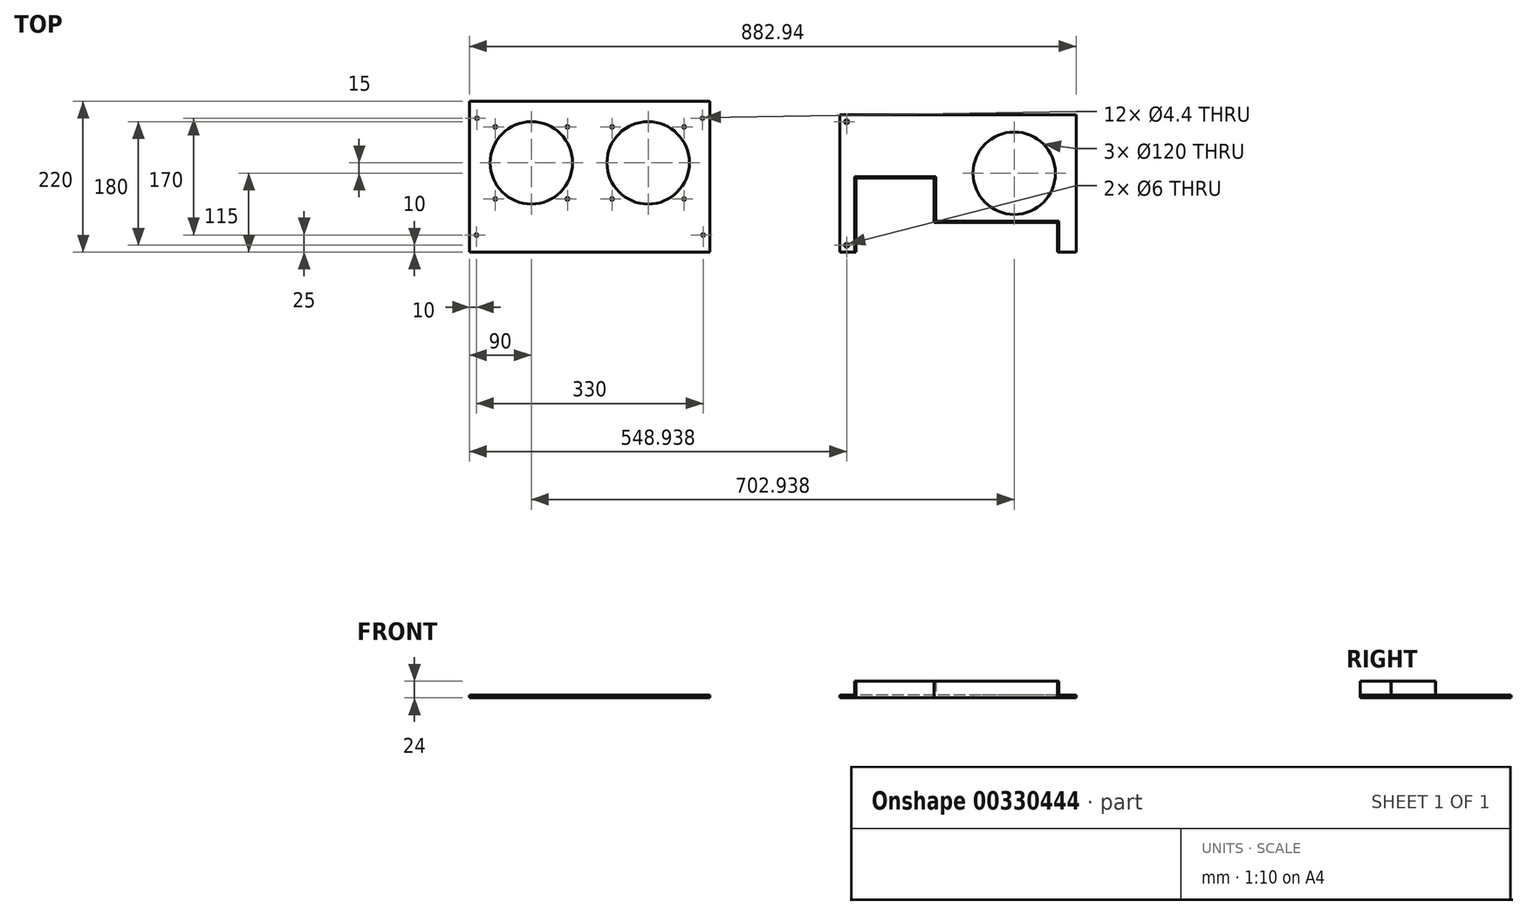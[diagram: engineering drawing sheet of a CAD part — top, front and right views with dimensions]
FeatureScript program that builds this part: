
annotation { "Feature Type Name" : "Feature", "Feature Type Description" : "" }
export const myFeature = defineFeature(function(context is Context, id is Id, definition is map)
    precondition{}
    {
        {
            var Q0;
            Q0=qCreatedBy(makeId("Top.planeOp"),FACE);
            var sketch = newSketch(context, id + "F0", { "sketchPlane" : qUnion([Q0])});
            skLineSegment(sketch, "E0.bottom", {"start": v(0, 0) * mm, "end": v(-350, 0) * mm});
            skLineSegment(sketch, "E0.top", {"start": v(0, 220) * mm, "end": v(-350, 220) * mm});
            skLineSegment(sketch, "E0.left", {"start": v(0, 0) * mm, "end": v(0, 220) * mm});
            skLineSegment(sketch, "E0.right", {"start": v(-350, 0) * mm, "end": v(-350, 220) * mm});
            skPoint(sketch, "E1", {"position": v(-339.2, 220) * mm});
            skPoint(sketch, "E2", {"position": v(-350, 195) * mm});
            skPoint(sketch, "E3", {"position": v(-339.2, 195) * mm});
            skCircle(sketch, "E4", {"center": v(-339.2, 195) * mm, "radius": 2.2 * mm});
            skPoint(sketch, "E5.endSnap0", {"position": v(-350, 110) * mm});
            skCircle(sketch, "E6.MirrorC", {"center": v(-340, 25) * mm, "radius": 2.2 * mm});
            skCircle(sketch, "E7.MirrorC", {"center": v(-10, 25) * mm, "radius": 2.2 * mm});
            skPoint(sketch, "E8.MirrorP", {"position": v(-10.8, 195) * mm});
            skCircle(sketch, "E9.MirrorC", {"center": v(-10.8, 195) * mm, "radius": 2.2 * mm});
            skLineSegment(sketch, "E10", {"start": v(-350, 110) * mm, "end": v(0, 110) * mm, "construction": true});
            skPoint(sketch, "E11", {"position": v(-270, 110) * mm});
            skPoint(sketch, "E12", {"position": v(-80, 110) * mm});
            skCircle(sketch, "E13", {"center": v(-260, 130) * mm, "radius": 60 * mm});
            skCircle(sketch, "E14", {"center": v(-90, 130) * mm, "radius": 60 * mm});
            skLineSegment(sketch, "E15", {"start": v(-260, 130) * mm, "end": v(-260, 220) * mm, "construction": true});
            skLineSegment(sketch, "E16", {"start": v(-260, 130) * mm, "end": v(-232.6, 130) * mm, "construction": true});
            skCircle(sketch, "E17", {"center": v(-312.5, 182.5) * mm, "radius": 2.2 * mm});
            skCircle(sketch, "E18.MirrorC", {"center": v(-207.5, 182.5) * mm, "radius": 2.2 * mm});
            skCircle(sketch, "E19.MirrorC", {"center": v(-312.5, 77.5) * mm, "radius": 2.2 * mm});
            skCircle(sketch, "E20.MirrorC", {"center": v(-207.5, 77.5) * mm, "radius": 2.2 * mm});
            skLineSegment(sketch, "E21", {"start": v(-175, 0) * mm, "end": v(-175, 35.85) * mm, "construction": true});
            skPoint(sketch, "E21.endSnap0", {"position": v(-175, 0) * mm});
            skCircle(sketch, "E22.MirrorC", {"center": v(-142.5, 77.5) * mm, "radius": 2.2 * mm});
            skCircle(sketch, "E23.MirrorC", {"center": v(-142.5, 182.5) * mm, "radius": 2.2 * mm});
            skCircle(sketch, "E24.MirrorC", {"center": v(-37.5, 182.5) * mm, "radius": 2.2 * mm});
            skCircle(sketch, "E25.MirrorC", {"center": v(-37.5, 77.5) * mm, "radius": 2.2 * mm});
            skSolve(sketch);
        }
        {
            var Q0;
            Q0=makeQuery(id+"F0.imprint","IMPRINT",FACE,{"disambiguationData":[TD([[makeQuery(id+"F0.imprint","IMPRINT",EDGE,{"derivedFrom":sQuery(id+"F0.wireOp",EDGE,"E0.bottom")}),-1.0]])]});
            extrude(context, id + "F1", {"entities" : qUnion([Q0]), "depth" : 4 * mm});
        }
        {
            var Q0;
            Q0=qCreatedBy(makeId("Top.planeOp"),FACE);
            var sketch = newSketch(context, id + "F2", { "sketchPlane" : qUnion([Q0])});
            skLineSegment(sketch, "E26.bottom", {"start": v(532.94, 0) * mm, "end": v(188.94, 0) * mm});
            skLineSegment(sketch, "E26.top", {"start": v(532.94, 200) * mm, "end": v(188.94, 200) * mm});
            skLineSegment(sketch, "E26.left", {"start": v(532.94, 0) * mm, "end": v(532.94, 200) * mm});
            skLineSegment(sketch, "E26.right", {"start": v(188.94, 0) * mm, "end": v(188.94, 200) * mm});
            skPoint(sketch, "E27", {"position": v(198.94, 200) * mm});
            skPoint(sketch, "E28", {"position": v(188.94, 190) * mm});
            skPoint(sketch, "E29", {"position": v(198.94, 190) * mm});
            skCircle(sketch, "E30", {"center": v(198.94, 190) * mm, "radius": 3 * mm});
            skPoint(sketch, "E31.endSnap0", {"position": v(360.94, 0) * mm});
            skLineSegment(sketch, "E32", {"start": v(188.94, 100) * mm, "end": v(210.85, 100) * mm, "construction": true});
            skPoint(sketch, "E32.endSnap0", {"position": v(188.94, 100) * mm});
            skCircle(sketch, "E33.MirrorC", {"center": v(198.94, 10) * mm, "radius": 3 * mm});
            skCircle(sketch, "E34.MirrorC", {"center": v(492.94, 10) * mm, "radius": 3 * mm});
            skPoint(sketch, "E35.MirrorP", {"position": v(492.94, 190) * mm});
            skLineSegment(sketch, "E36", {"start": v(507.94, 45) * mm, "end": v(507.94, 0) * mm});
            skLineSegment(sketch, "E37", {"start": v(507.94, 45) * mm, "end": v(328.46, 45) * mm});
            skLineSegment(sketch, "E38", {"start": v(328.46, 45) * mm, "end": v(328.46, 110) * mm});
            skLineSegment(sketch, "E39", {"start": v(328.46, 110) * mm, "end": v(210.44, 110) * mm});
            skLineSegment(sketch, "E40", {"start": v(210.44, 110) * mm, "end": v(210.44, 0) * mm});
            skLineSegment(sketch, "E41.0", {"start": v(212.44, 108) * mm, "end": v(212.44, 0) * mm});
            skLineSegment(sketch, "E41.1", {"start": v(505.94, 43) * mm, "end": v(505.94, 3) * mm});
            skLineSegment(sketch, "E41.2", {"start": v(505.94, 43) * mm, "end": v(326.46, 43) * mm});
            skLineSegment(sketch, "E41.3", {"start": v(326.46, 43) * mm, "end": v(326.46, 108) * mm});
            skLineSegment(sketch, "E41.4", {"start": v(326.46, 108) * mm, "end": v(212.44, 108) * mm});
            skLineSegment(sketch, "E42", {"start": v(505.94, 3) * mm, "end": v(505.94, 0) * mm});
            skPoint(sketch, "E43", {"position": v(507.94, 115) * mm});
            skPoint(sketch, "E44", {"position": v(442.94, 115) * mm});
            skCircle(sketch, "E45", {"center": v(442.94, 115) * mm, "radius": 60 * mm});
            skSolve(sketch);
        }
        {
            var Q0;
            Q0=makeQuery(id+"F2.imprint","IMPRINT",FACE,{"disambiguationData":[TD([[makeQuery(id+"F2.imprint","IMPRINT",EDGE,{"derivedFrom":sQuery(id+"F2.wireOp",EDGE,"E26.top")}),1.0]])]});
            extrude(context, id + "F3", {"entities" : qUnion([Q0]), "depth" : 4 * mm});
        }
        {
            var Q0;
            {var subQ3=sQuery(id+"F2.wireOp",EDGE,"E36");Q0=makeQuery(id+"F2.imprint","IMPRINT",FACE,{"disambiguationData":[TD([[makeQuery(id+"F2.imprint","IMPRINT",EDGE,{"derivedFrom":subQ3}),-1.0]])]});}
            extrude(context, id + "F4", {"entities" : qUnion([Q0]), "operationType" : NewBodyOperationType.ADD, "depth" : 24 * mm});
        }
    });
